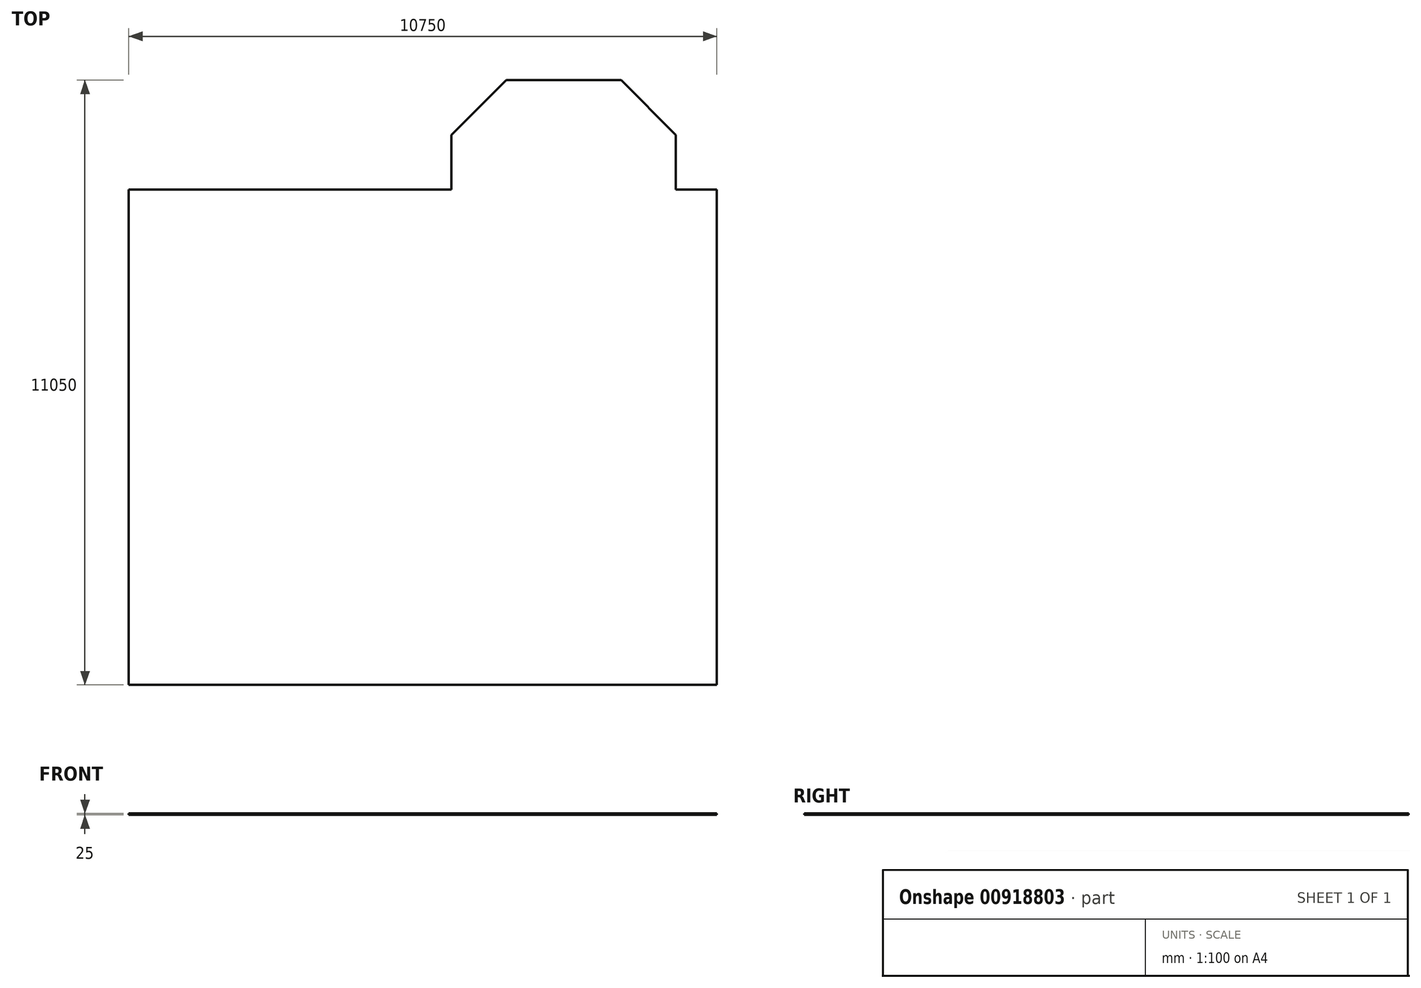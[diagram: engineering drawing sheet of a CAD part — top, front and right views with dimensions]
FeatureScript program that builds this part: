
annotation { "Feature Type Name" : "Feature", "Feature Type Description" : "" }
export const myFeature = defineFeature(function(context is Context, id is Id, definition is map)
    precondition{}
    {
        {
            var Q0;
            Q0=qCreatedBy(makeId("Top.planeOp"),FACE);
            var sketch = newSketch(context, id + "F0", { "sketchPlane" : qUnion([Q0])});
            skLineSegment(sketch, "E0.bottom", {"start": v(5375, -4525) * mm, "end": v(-5375, -4525) * mm});
            skLineSegment(sketch, "E0.top", {"start": v(5375, 4525) * mm, "end": v(-5375, 4525) * mm});
            skLineSegment(sketch, "E0.left", {"start": v(5375, -4525) * mm, "end": v(5375, 4525) * mm});
            skLineSegment(sketch, "E0.right", {"start": v(-5375, -4525) * mm, "end": v(-5375, 4525) * mm});
            skPoint(sketch, "E0.middle", {"position": v(0, 0) * mm});
            skLineSegment(sketch, "E1", {"start": v(525, 4525) * mm, "end": v(525, 5525) * mm});
            skLineSegment(sketch, "E2", {"start": v(525, 5525) * mm, "end": v(1525, 6525) * mm});
            skLineSegment(sketch, "E3", {"start": v(4625, 5525) * mm, "end": v(4625, 4525) * mm});
            skLineSegment(sketch, "E4", {"start": v(1525, 6525) * mm, "end": v(3625, 6525) * mm});
            skLineSegment(sketch, "E5", {"start": v(3625, 6525) * mm, "end": v(4625, 5525) * mm});
            skSolve(sketch);
        }
        {
            var Q0;
            Q0=makeQuery(id+"F0.imprint","IMPRINT",FACE,{"disambiguationData":[TD([[makeQuery(id+"F0.imprint","IMPRINT",EDGE,{"derivedFrom":sQuery(id+"F0.wireOp",EDGE,"E0.bottom")}),-1.0]])]});
            var Q1;
            {var subQ1=sQuery(id+"F0.wireOp",EDGE,"E1");Q1=makeQuery(id+"F0.imprint","IMPRINT",FACE,{"disambiguationData":[TD([[makeQuery(id+"F0.imprint","IMPRINT",EDGE,{"derivedFrom":subQ1}),-1.0]])]});}
            extrude(context, id + "F1", {"entities" : qUnion([Q0, Q1]), "depth" : 25 * mm, "offsetDistance" : 25 * mm});
        }
    });
